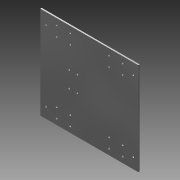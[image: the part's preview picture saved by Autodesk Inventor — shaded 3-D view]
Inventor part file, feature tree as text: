
AUTODESK INVENTOR PART (.ipt)
format: ipt  version: 2015 (Build 190159000, 159)  size: 129,024 bytes
history: native  units: mm
features: extrude x3, sketch x3, mirror x2
ambient origin geometry x8: Origin, YZ Plane, XZ Plane, XY Plane, X Axis, Y Axis, Z Axis, Center Point
bodies: Solid1 (feature_tree)
feature tree (8):
  extrude  "Extrusion1"  Depth=4.125mm
  extrude  "Extrusion2"  Depth=25.0mm
  mirror  "Mirror1"
  mirror  "Mirror2"
  extrude  "Extrusion3"  Depth=10.0mm
  sketch  "Sketch1"  dims[d3=0.0mm d4=4.125mm]
  sketch  "Sketch2"  dims[d5=18.0mm d6=25.0mm]
  sketch  "Sketch3"  dims[d7=29.5mm d8=11.0mm d9=4.125mm d10=10.0mm d11=20.0mm d12=10.0mm d13=0.0mm d14=30.0mm d15=4.125mm d16=15.0mm d17=60.0mm d18=10.0mm d19=0.0mm]
